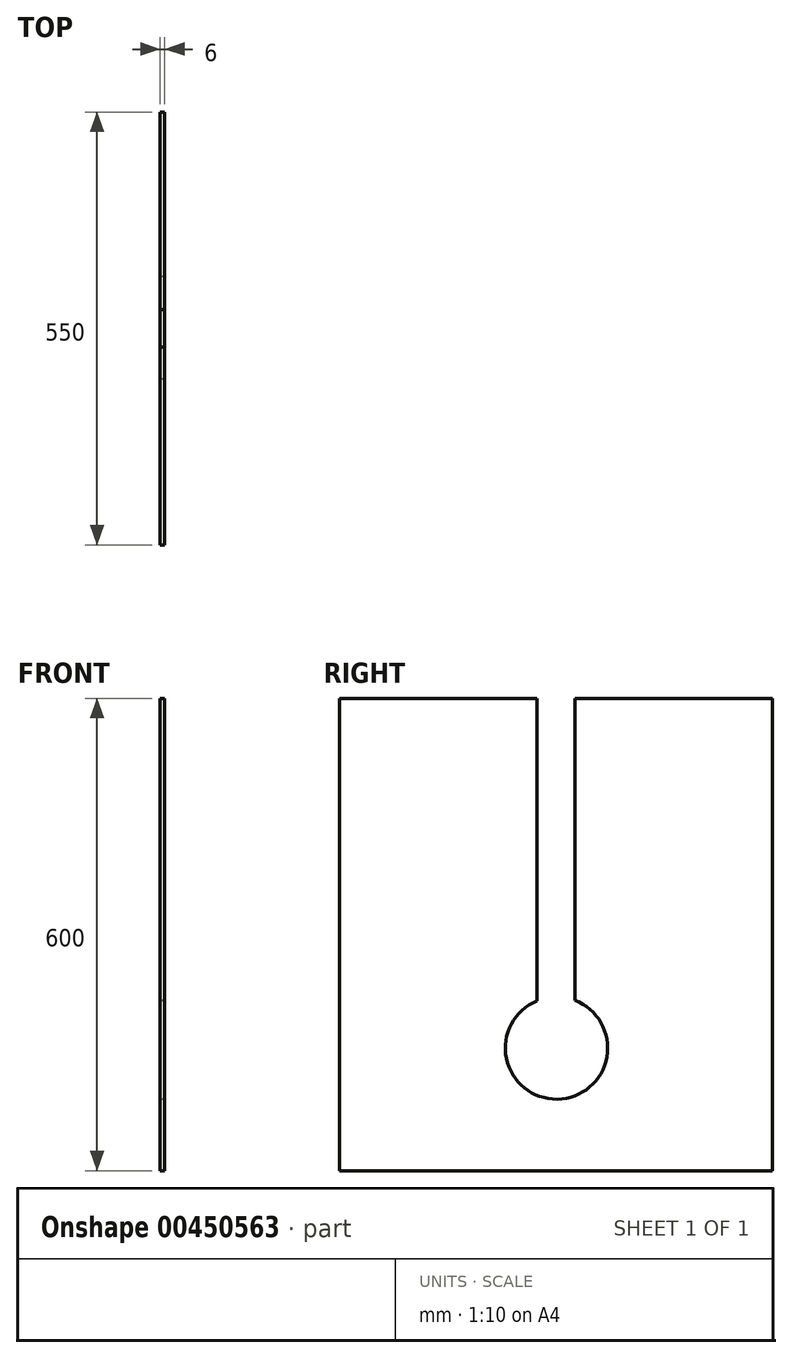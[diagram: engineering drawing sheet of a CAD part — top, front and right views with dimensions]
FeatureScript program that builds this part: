
annotation { "Feature Type Name" : "Feature", "Feature Type Description" : "" }
export const myFeature = defineFeature(function(context is Context, id is Id, definition is map)
    precondition{}
    {
        {
            var Q0;
            Q0=qCreatedBy(makeId("Right.planeOp"),FACE);
            var sketch = newSketch(context, id + "F0", { "sketchPlane" : qUnion([Q0])});
            skLineSegment(sketch, "E0.top", {"start": v(0, -24.71) * mm, "end": v(550, -24.71) * mm});
            skLineSegment(sketch, "E0.left", {"start": v(0, 575.29) * mm, "end": v(0, -24.71) * mm});
            skLineSegment(sketch, "E0.right", {"start": v(550, 575.29) * mm, "end": v(550, -24.71) * mm});
            skLineSegment(sketch, "E1", {"start": v(550, 575.29) * mm, "end": v(299, 575.29) * mm});
            skLineSegment(sketch, "E2", {"start": v(251, 575.22) * mm, "end": v(251, 191.1) * mm});
            skLineSegment(sketch, "E3", {"start": v(299, 575.29) * mm, "end": v(299, 191.78) * mm});
            skArc(sketch, "E4", {"start": v(251, 191.1) * mm, "mid": v(276.76, 66.05) * mm, "end": v(299, 191.78) * mm});
            skLineSegment(sketch, "E5", {"start": v(0, 575.29) * mm, "end": v(251, 575.22) * mm});
            skSolve(sketch);
        }
        {
            var Q0;
            Q0=makeQuery(id+"F0.imprint","IMPRINT",FACE,{"disambiguationData":[TD([[makeQuery(id+"F0.imprint","IMPRINT",EDGE,{"derivedFrom":sQuery(id+"F0.wireOp",EDGE,"E0.top")}),1.0]])]});
            extrude(context, id + "F1", {"entities" : qUnion([Q0]), "depth" : 6 * mm});
        }
    });
